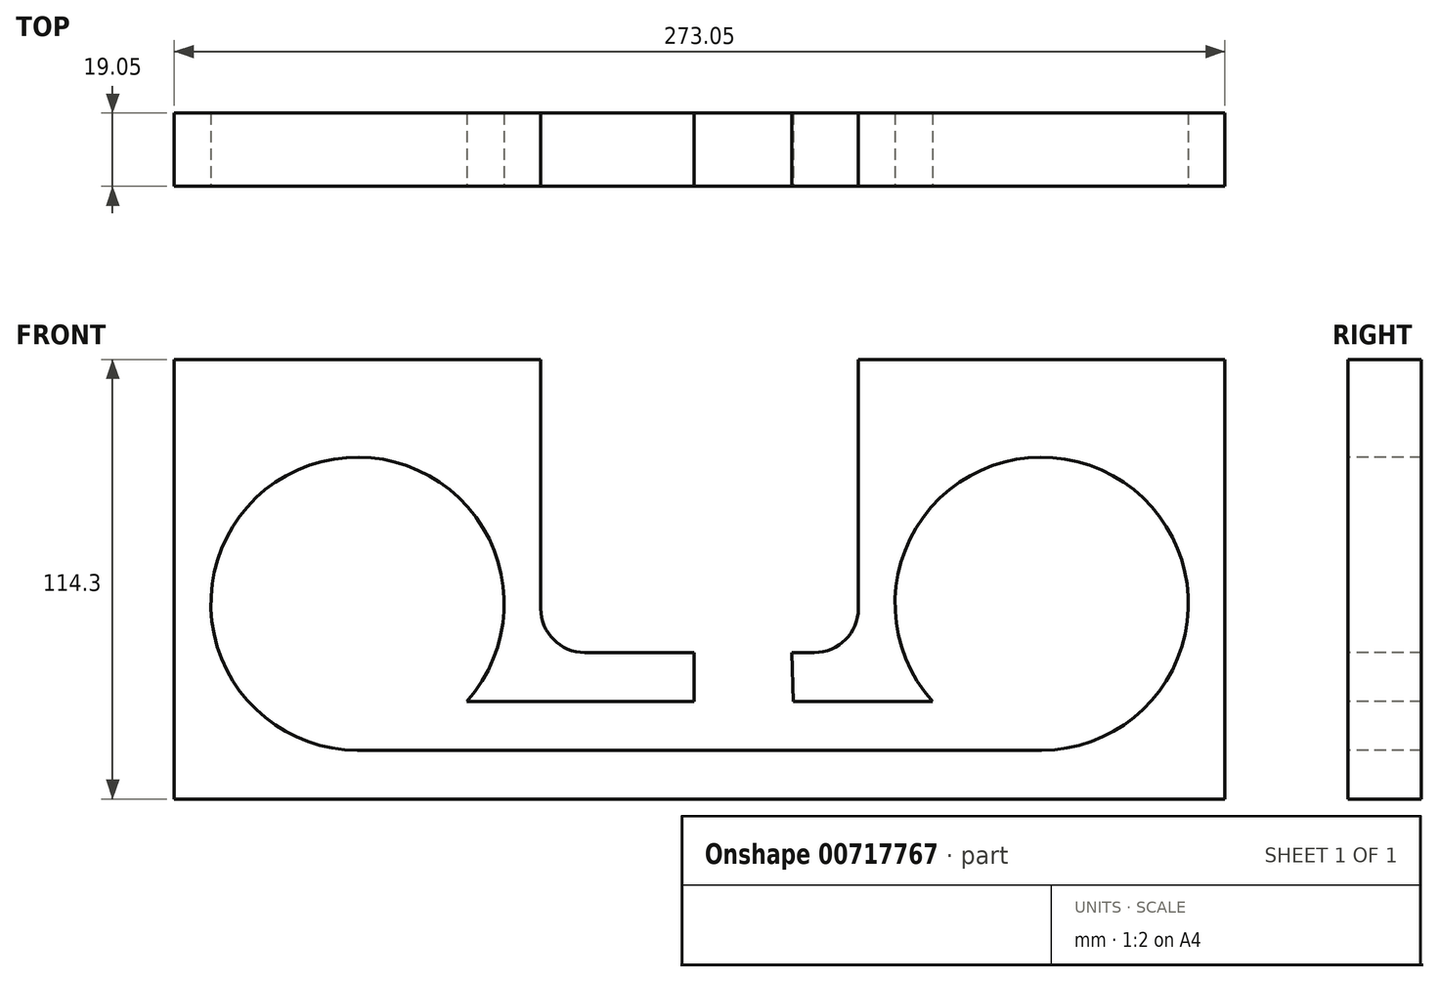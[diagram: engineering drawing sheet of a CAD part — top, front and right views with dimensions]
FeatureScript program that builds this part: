
annotation { "Feature Type Name" : "Feature", "Feature Type Description" : "" }
export const myFeature = defineFeature(function(context is Context, id is Id, definition is map)
    precondition{}
    {
        {
            var Q0;
            Q0=qCreatedBy(makeId("Front.planeOp"),FACE);
            var sketch = newSketch(context, id + "F0", { "sketchPlane" : qUnion([Q0])});
            skLineSegment(sketch, "E0.bottom", {"start": v(0, 0) * mm, "end": v(273.05, 0) * mm});
            skLineSegment(sketch, "E0.top", {"start": v(0, 114.3) * mm, "end": v(273.05, 114.3) * mm});
            skLineSegment(sketch, "E0.left", {"start": v(0, 0) * mm, "end": v(0, 114.3) * mm});
            skLineSegment(sketch, "E0.right", {"start": v(273.05, 0) * mm, "end": v(273.05, 114.3) * mm});
            skSolve(sketch);
        }
        {
            var Q0;
            Q0=makeQuery(id+"F0.imprint","IMPRINT",FACE,{"disambiguationData":[TD([[makeQuery(id+"F0.imprint","IMPRINT",EDGE,{"derivedFrom":sQuery(id+"F0.wireOp",EDGE,"E0.bottom")}),1.0]])]});
            extrude(context, id + "F1", {"entities" : qUnion([Q0]), "depth" : 19.05 * mm, "offsetDistance" : 25.4 * mm});
        }
        {
            var Q0;
            Q0=makeQuery(id+"F1.opExtrude","CAP_FACE",FACE,{"disambiguationData":[OSD([sQuery(id+"F0.wireOp",EDGE,"E0.bottom"),sQuery(id+"F0.wireOp",EDGE,"E0.top"),sQuery(id+"F0.wireOp",EDGE,"E0.left"),sQuery(id+"F0.wireOp",EDGE,"E0.right")])],"isStart":false});
            var sketch = newSketch(context, id + "F2", { "sketchPlane" : qUnion([Q0])});
            skCircle(sketch, "E1", {"center": v(47.63, 50.8) * mm, "radius": 38.1 * mm});
            skCircle(sketch, "E2", {"center": v(225.43, 50.8) * mm, "radius": 38.1 * mm});
            skSolve(sketch);
        }
        {
            var Q0;
            Q0=makeQuery(id+"F2.imprint","IMPRINT",FACE,{"disambiguationData":[TD([[makeQuery(id+"F2.imprint","IMPRINT",EDGE,{"derivedFrom":sQuery(id+"F2.wireOp",EDGE,"E1")}),1.0]])]});
            var Q1;
            Q1=makeQuery(id+"F2.imprint","IMPRINT",FACE,{"disambiguationData":[TD([[makeQuery(id+"F2.imprint","IMPRINT",EDGE,{"derivedFrom":sQuery(id+"F2.wireOp",EDGE,"E2")}),1.0]])]});
            extrude(context, id + "F3", {"entities" : qUnion([Q0, Q1]), "operationType" : NewBodyOperationType.REMOVE, "oppositeDirection" : true, "depth" : 25.4 * mm, "offsetDistance" : 25.4 * mm});
        }
        {
            var Q0;
            Q0=makeQuery(id+"F1.opExtrude","CAP_FACE",FACE,{"disambiguationData":[OSD([sQuery(id+"F0.wireOp",EDGE,"E0.bottom"),sQuery(id+"F0.wireOp",EDGE,"E0.top"),sQuery(id+"F0.wireOp",EDGE,"E0.left"),sQuery(id+"F0.wireOp",EDGE,"E0.right")])],"isStart":false});
            var sketch = newSketch(context, id + "F4", { "sketchPlane" : qUnion([Q0])});
            skLineSegment(sketch, "E3", {"start": v(95.25, 114.3) * mm, "end": v(95.25, 49.53) * mm});
            skLineSegment(sketch, "E4", {"start": v(106.68, 38.1) * mm, "end": v(166.37, 38.1) * mm});
            skLineSegment(sketch, "E5", {"start": v(177.8, 49.53) * mm, "end": v(177.8, 114.3) * mm});
            skLineSegment(sketch, "E6", {"start": v(95.25, 114.3) * mm, "end": v(177.8, 114.3) * mm});
            skPoint(sketch, "E7.visualSharp", {"position": v(95.25, 38.1) * mm});
            skArc(sketch, "E7.filletArc", {"start": v(95.25, 49.53) * mm, "mid": v(98.6, 41.45) * mm, "end": v(106.68, 38.1) * mm});
            skPoint(sketch, "E8.visualSharp", {"position": v(177.8, 38.1) * mm});
            skArc(sketch, "E8.filletArc", {"start": v(166.37, 38.1) * mm, "mid": v(174.45, 41.45) * mm, "end": v(177.8, 49.53) * mm});
            skSolve(sketch);
        }
        {
            var Q0;
            Q0=makeQuery(id+"F4.imprint","IMPRINT",FACE,{"disambiguationData":[TD([[makeQuery(id+"F4.imprint","IMPRINT",EDGE,{"derivedFrom":sQuery(id+"F4.wireOp",EDGE,"E3")}),1.0]])]});
            extrude(context, id + "F5", {"entities" : qUnion([Q0]), "operationType" : NewBodyOperationType.REMOVE, "oppositeDirection" : true, "depth" : 25.4 * mm, "offsetDistance" : 25.4 * mm});
        }
        {
            var Q0;
            Q0=makeQuery(id+"F1.opExtrude","CAP_FACE",FACE,{"disambiguationData":[OSD([sQuery(id+"F0.wireOp",EDGE,"E0.bottom"),sQuery(id+"F0.wireOp",EDGE,"E0.top"),sQuery(id+"F0.wireOp",EDGE,"E0.left"),sQuery(id+"F0.wireOp",EDGE,"E0.right")])],"isStart":false});
            var sketch = newSketch(context, id + "F6", { "sketchPlane" : qUnion([Q0])});
            skLineSegment(sketch, "E9", {"start": v(160.55, 38.1) * mm, "end": v(135.15, 38.1) * mm});
            skLineSegment(sketch, "E10", {"start": v(135.15, 38.1) * mm, "end": v(135.15, 25.4) * mm});
            skLineSegment(sketch, "E11", {"start": v(135.15, 25.4) * mm, "end": v(76.02, 25.4) * mm});
            skLineSegment(sketch, "E12", {"start": v(76.02, 25.4) * mm, "end": v(47.63, 12.7) * mm});
            skLineSegment(sketch, "E13", {"start": v(47.63, 12.7) * mm, "end": v(225.43, 12.7) * mm});
            skLineSegment(sketch, "E14", {"start": v(225.43, 12.7) * mm, "end": v(197.03, 25.4) * mm});
            skLineSegment(sketch, "E15", {"start": v(197.03, 25.4) * mm, "end": v(160.86, 25.4) * mm});
            skLineSegment(sketch, "E16", {"start": v(160.86, 25.4) * mm, "end": v(160.55, 38.1) * mm});
            skSolve(sketch);
        }
        {
            var Q0;
            Q0=makeQuery(id+"F6.imprint","IMPRINT",FACE,{"disambiguationData":[TD([[makeQuery(id+"F6.imprint","IMPRINT",EDGE,{"derivedFrom":sQuery(id+"F6.wireOp",EDGE,"E9")}),-1.0]])]});
            extrude(context, id + "F7", {"entities" : qUnion([Q0]), "operationType" : NewBodyOperationType.REMOVE, "oppositeDirection" : true, "depth" : 25.4 * mm, "offsetDistance" : 25.4 * mm});
        }
    });
